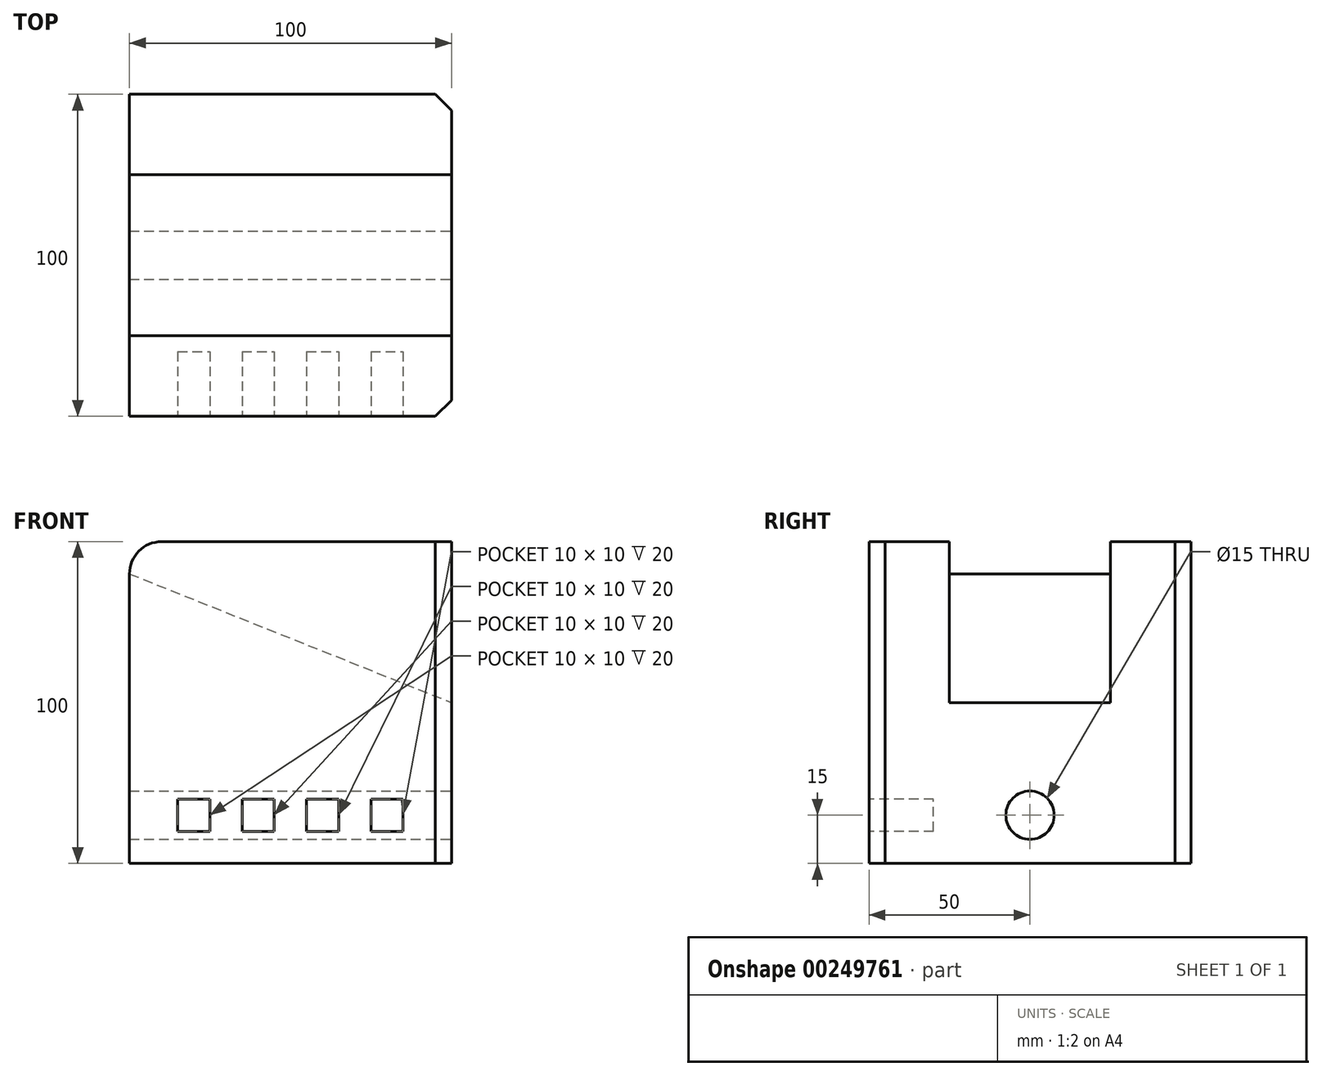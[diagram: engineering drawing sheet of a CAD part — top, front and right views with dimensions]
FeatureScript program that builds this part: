
annotation { "Feature Type Name" : "Feature", "Feature Type Description" : "" }
export const myFeature = defineFeature(function(context is Context, id is Id, definition is map)
    precondition{}
    {
        {
            var Q0;
            Q0=qCreatedBy(makeId("Top.planeOp"),FACE);
            var sketch = newSketch(context, id + "F0", { "sketchPlane" : qUnion([Q0])});
            skLineSegment(sketch, "E0.bottom", {"start": v(0, 0) * mm, "end": v(100, 0) * mm});
            skLineSegment(sketch, "E0.top", {"start": v(0, 100) * mm, "end": v(100, 100) * mm});
            skLineSegment(sketch, "E0.left", {"start": v(0, 0) * mm, "end": v(0, 100) * mm});
            skLineSegment(sketch, "E0.right", {"start": v(100, 0) * mm, "end": v(100, 100) * mm});
            skSolve(sketch);
        }
        {
            var Q0;
            Q0 = qSketchRegion(id + "F0", true);
            extrude(context, id + "F1", {"entities" : qUnion([Q0]), "depth" : 100 * mm});
        }
        {
            var Q0;
            Q0=makeQuery(id+"F1.opExtrude","CAP_FACE",FACE,{"disambiguationData":[OSD([sQuery(id+"F0.wireOp",EDGE,"E0.bottom"),sQuery(id+"F0.wireOp",EDGE,"E0.top"),sQuery(id+"F0.wireOp",EDGE,"E0.left"),sQuery(id+"F0.wireOp",EDGE,"E0.right")])],"isStart":false});
            var sketch = newSketch(context, id + "F2", { "sketchPlane" : qUnion([Q0])});
            skLineSegment(sketch, "E1", {"start": v(0, 50) * mm, "end": v(100, 50) * mm, "construction": true});
            skSolve(sketch);
        }
        {
            var Q0;
            Q0=makeQuery(id+"F1.opExtrude","CAP_EDGE",EDGE,{"disambiguationData":[OSD([sQuery(id+"F0.wireOp",EDGE,"E0.left")])],"isStart":false});
            fillet(context, id + "F3", {"entities" : qUnion([Q0]), "radius" : 10 * mm, "tangentPropagation" : true, "allowEdgeOverflow" : false});
        }
        {
            var Q0;
            Q0=makeQuery(id+"F1.opExtrude","SWEPT_FACE",FACE,{"disambiguationData":[OSD([sQuery(id+"F0.wireOp",EDGE,"E0.bottom")])]});
            var sketch = newSketch(context, id + "F4", { "sketchPlane" : qUnion([Q0])});
            skLineSegment(sketch, "E2.bottom", {"start": v(15, 10) * mm, "end": v(25, 10) * mm});
            skLineSegment(sketch, "E2.top", {"start": v(15, 20) * mm, "end": v(25, 20) * mm});
            skLineSegment(sketch, "E2.left", {"start": v(15, 10) * mm, "end": v(15, 20) * mm});
            skLineSegment(sketch, "E2.right", {"start": v(25, 10) * mm, "end": v(25, 20) * mm});
            skLineSegment(sketch, "E3.1.0.0", {"start": v(35, 20) * mm, "end": v(45, 20) * mm});
            skLineSegment(sketch, "E3.1.0.1", {"start": v(45, 10) * mm, "end": v(45, 20) * mm});
            skLineSegment(sketch, "E3.1.0.2", {"start": v(35, 10) * mm, "end": v(45, 10) * mm});
            skLineSegment(sketch, "E3.1.0.3", {"start": v(35, 10) * mm, "end": v(35, 20) * mm});
            skLineSegment(sketch, "E3.2.0.0", {"start": v(55, 20) * mm, "end": v(65, 20) * mm});
            skLineSegment(sketch, "E3.2.0.1", {"start": v(65, 10) * mm, "end": v(65, 20) * mm});
            skLineSegment(sketch, "E3.2.0.2", {"start": v(55, 10) * mm, "end": v(65, 10) * mm});
            skLineSegment(sketch, "E3.2.0.3", {"start": v(55, 10) * mm, "end": v(55, 20) * mm});
            skLineSegment(sketch, "E3.3.0.0", {"start": v(75, 20) * mm, "end": v(85, 20) * mm});
            skLineSegment(sketch, "E3.3.0.1", {"start": v(85, 10) * mm, "end": v(85, 20) * mm});
            skLineSegment(sketch, "E3.3.0.2", {"start": v(75, 10) * mm, "end": v(85, 10) * mm});
            skLineSegment(sketch, "E3.3.0.3", {"start": v(75, 10) * mm, "end": v(75, 20) * mm});
            skLineSegment(sketch, "E3.direction1", {"start": v(15, 20) * mm, "end": v(35, 20) * mm, "construction": true});
            skSolve(sketch);
        }
        {
            var Q0;
            Q0 = qSketchRegion(id + "F4", true);
            extrude(context, id + "F5", {"entities" : qUnion([Q0]), "operationType" : NewBodyOperationType.REMOVE, "oppositeDirection" : true, "depth" : 20 * mm});
        }
        {
            var Q0;
            Q0=makeQuery(id+"F1.opExtrude","SWEPT_FACE",FACE,{"disambiguationData":[OSD([sQuery(id+"F0.wireOp",EDGE,"E0.right")])]});
            var sketch = newSketch(context, id + "F6", { "sketchPlane" : qUnion([Q0])});
            skCircle(sketch, "E4", {"center": v(50, 15) * mm, "radius": 7.5 * mm});
            skSolve(sketch);
        }
        {
            var Q0;
            Q0 = qSketchRegion(id + "F6", true);
            extrude(context, id + "F7", {"entities" : qUnion([Q0]), "operationType" : NewBodyOperationType.REMOVE, "endBound" : BoundingType.THROUGH_ALL, "oppositeDirection" : true, "depth" : 25 * mm});
        }
        {
            var Q0;
            Q0=qCreatedBy(makeId("Front.planeOp"),FACE);
            cPlane(context, id + "F8", {"entities" : qUnion([Q0]), "cplaneType" : CPlaneType.OFFSET, "offset" : 50 * mm, "oppositeDirection" : true, "width" : 150 * mm, "height" : 150 * mm});
        }
        {
            var Q0;
            Q0=qCreatedBy(id+"F8.planeOp",FACE);
            var sketch = newSketch(context, id + "F9", { "sketchPlane" : qUnion([Q0])});
            skLineSegment(sketch, "E5", {"start": v(100, 50) * mm, "end": v(100, 100) * mm});
            skLineSegment(sketch, "E6", {"start": v(100, 100) * mm, "end": v(0, 100) * mm});
            skLineSegment(sketch, "E7", {"start": v(0, 100) * mm, "end": v(0, 90) * mm});
            skLineSegment(sketch, "E8", {"start": v(0, 90) * mm, "end": v(100, 50) * mm});
            skSolve(sketch);
        }
        {
            var Q0;
            Q0 = qSketchRegion(id + "F9", true);
            extrude(context, id + "F10", {"entities" : qUnion([Q0]), "operationType" : NewBodyOperationType.REMOVE, "endBound" : BoundingType.SYMMETRIC, "oppositeDirection" : true, "depth" : 50 * mm});
        }
        {
            var Q0;
            Q0=makeQuery(id+"F1.opExtrude","SWEPT_EDGE",EDGE,{"disambiguationData":[OSD([sQuery(id+"F0.wireOp",EDGE,"E0.bottom"),sQuery(id+"F0.wireOp",EDGE,"E0.right")])]});
            var Q1;
            Q1=makeQuery(id+"F1.opExtrude","SWEPT_EDGE",EDGE,{"disambiguationData":[OSD([sQuery(id+"F0.wireOp",EDGE,"E0.top"),sQuery(id+"F0.wireOp",EDGE,"E0.right")])]});
            chamfer(context, id + "F11", {"entities" : qUnion([Q0, Q1]), "width" : 5 * mm, "tangentPropagation" : true});
        }
    });
